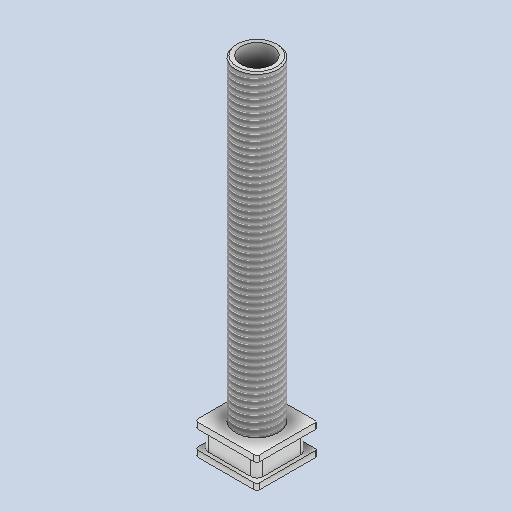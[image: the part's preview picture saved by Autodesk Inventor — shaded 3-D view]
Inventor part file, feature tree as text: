
AUTODESK INVENTOR PART (.ipt)
format: ipt  version: 2024.1 (Build 281209000, 209)  size: 402,432 bytes
history: native  units: in
note: dims shown in document units (in); Inventor stores cm internally (conversion verified against a paired STEP export)
features: extrude x2, thread x1, chamfer x1, sketch x1, imported_body x1
ambient origin geometry x8: Origin, YZ Plane, XZ Plane, XY Plane, X Axis, Y Axis, Z Axis, Center Point
bodies: Solid1 (feature_tree)
feature tree (6):
  extrude  "Extrusion2"  Depth=0.0098in
  extrude  "Extrusion3"  Depth=0.2756in
  thread  "Thread1"  [1 undecoded]
  chamfer  "Chamfer1"  Distance=1.9685in
  sketch  "Sketch2"  dims[d3=0.0in d4=0.0in d5=0.2047in d6=0.2756in d7=2.0472in d8=0.0in d9=1.9685in d10=0.0in d11=0.0098in d12=0.0787in d13=45.0deg]
  imported_body  "Base1"
note: 1 required parameter value undecoded (feature->parameter linkage not recoverable at this tier; creation-order binding heuristic only, values carry confidence <= 0.55)
